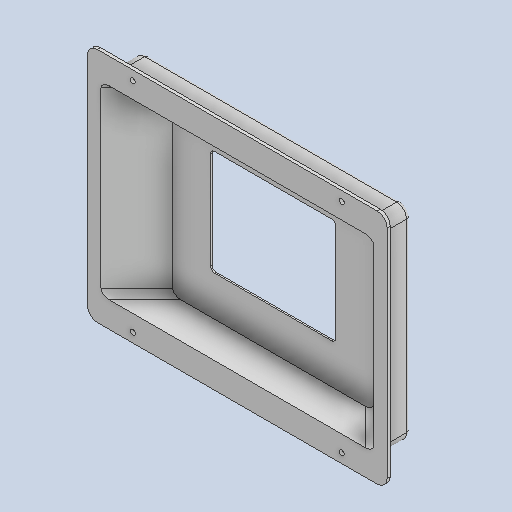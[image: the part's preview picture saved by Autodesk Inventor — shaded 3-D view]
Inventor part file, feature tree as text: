
AUTODESK INVENTOR PART (.ipt)
format: ipt  version: 2023 (Build 270158000, 158)  size: 158,208 bytes
history: native  units: in
note: dims shown in document units (in); Inventor stores cm internally (conversion verified against a paired STEP export)
features: other x1, sketch x1
ambient origin geometry x8: Origin, YZ Plane, XZ Plane, XY Plane, X Axis, Y Axis, Z Axis, Center Point
bodies: Solid2 (feature_tree), Solid1 (feature_tree)
feature tree (2):
  other  "Repaired Geometry1"
  sketch  "Sketch8"
